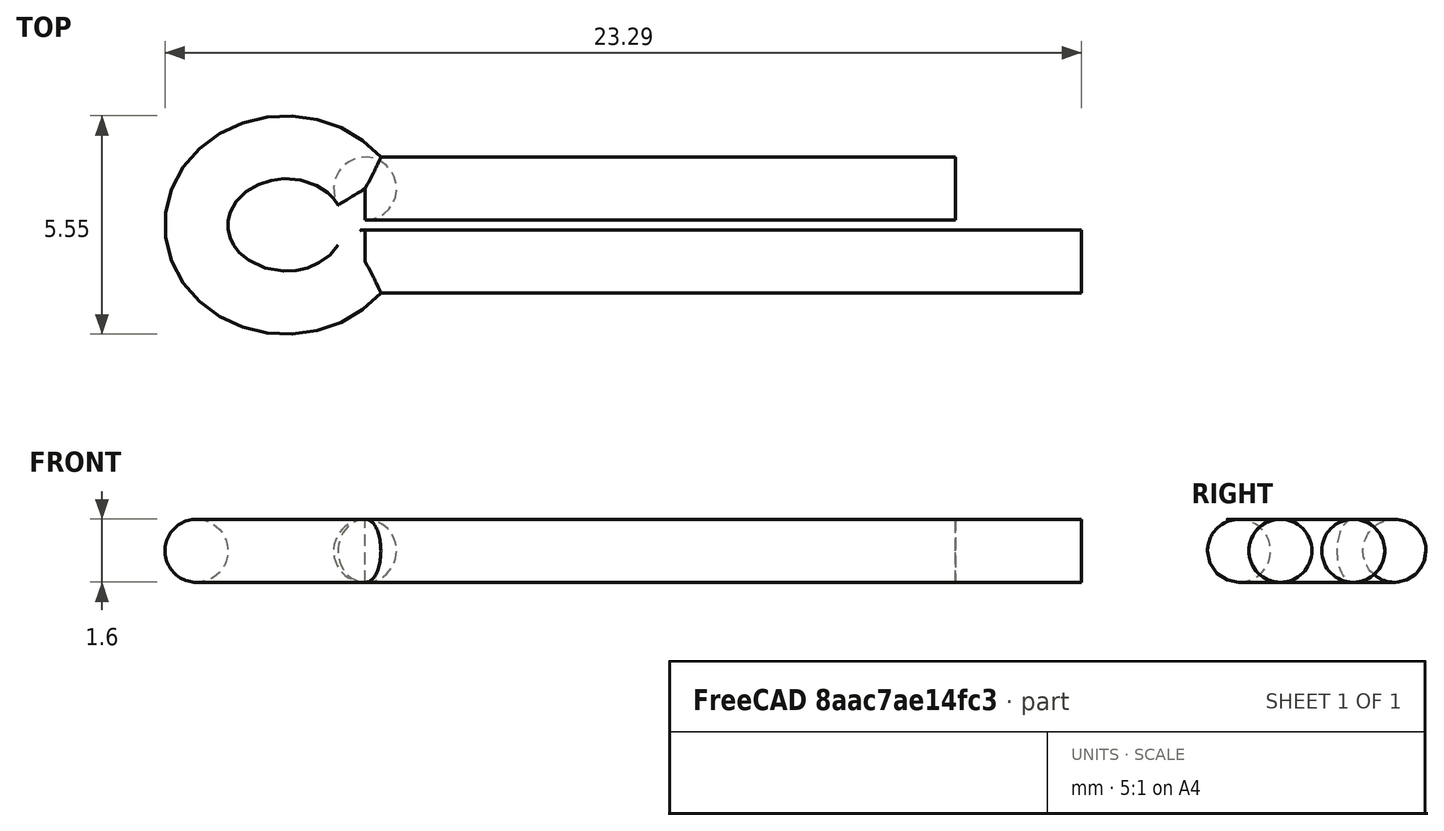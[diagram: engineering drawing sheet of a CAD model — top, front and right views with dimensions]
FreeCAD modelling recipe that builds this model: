
FCSTD DOCUMENT  (FreeCAD 0.17R11586 (Git))
Label: support pin
License: All rights reserved
LicenseURL: http://en.wikipedia.org/wiki/All_rights_reserved
objects: Sketcher::SketchObject×2, PartDesign::Plane×1, PartDesign::AdditivePipe×1, PartDesign::Body×1
note: 6 computed .brp shape members not serialized (recipe doc carries the construction recipe); baked Part::Feature solids carry a one-line shape summary decoded from their .brp

FEATURE [Sketcher::SketchObject] Sketch005
  MapMode = 5
  Placement = pos=(66.3738,51.9691,107.627) rot=(0,0,1;0rad)
  sketch-geometry (7):
    g0: ArcOfEllipse CenterX=-14.3187 CenterY=1.725 CenterZ=0 NormalX=0 NormalY=0 NormalZ=1 MajorRadius=2.275 MinorRadius=1.975 AngleXU=0 StartAngle=0.487427 EndAngle=5.79576
    g1: LineSegment [constr] StartX=-12.0437 StartY=1.725 StartZ=0 EndX=-16.5937 EndY=1.725 EndZ=0
    g2: LineSegment [constr] StartX=-14.3187 StartY=3.7 StartZ=0 EndX=-14.3187 EndY=-0.25 EndZ=0
    g3: GeomPoint X=-13.1895 Y=1.725 Z=0
    g4: GeomPoint X=-15.4478 Y=1.725 Z=0
    g5: LineSegment StartX=-12.3086 StartY=2.65 StartZ=0 EndX=2.6914 EndY=2.65 EndZ=0
    g6: LineSegment StartX=-12.3086 StartY=0.8 StartZ=0 EndX=5.8914 EndY=0.8 EndZ=0
  constraints (13):
    c: InternalAlignment(g1-g4 -> g0) x4
    c: Horizontal(g1)
    c: Horizontal(g5)
    c: Horizontal(g6)
    c: Coincident(g0,g5)
    c: DistanceX(g5,g6) = 3.2
    c: Coincident(g0,g6)
    c: Symmetric(g0,g0,g1)
    c: DistanceY(g0,g2) = 1.975
    c: DistanceX(g1,g0) = 2.275
    c: DistanceY(g6,g5) = 1.85
    c: DistanceX(g5,g5) = 15
    c: DistanceY(g-1,g6) = 0.8
FEATURE [PartDesign::Plane] DatumPlane002
  MapMode = 7
  Placement = pos=(72.2652,52.7691,107.627) rot=(0.57735,-0.57735,-0.57735;2.0944rad)
  Support = -> [Sketch005]
FEATURE [Sketcher::SketchObject] Sketch006
  MapMode = 5
  Placement = pos=(72.2652,52.7691,107.627) rot=(0.57735,-0.57735,-0.57735;2.0944rad)
  Support = -> [DatumPlane002]
  sketch-geometry (1):
    g0: Circle CenterX=0 CenterY=0 CenterZ=0 NormalX=0 NormalY=0 NormalZ=1 Radius=0.8
  constraints (2):
    c: Coincident(g0,g-1)
    c: Radius(g0) = 0.8
FEATURE [PartDesign::AdditivePipe] AdditivePipe
  AuxilleryCurvelinear = true
  AuxillerySpineTangent = false
  Binormal = (0,0,0)
  Mode = 0
  Placement = pos=(72.2652,52.7691,107.627) rot=(0.57735,-0.57735,-0.57735;2.0944rad)
  Profile = -> Sketch006
  Spine = -> Sketch005
  SpineTangent = false
  Transformation = 0
  Transition = 2
FEATURE [PartDesign::Body] Body
  Group = -> [Sketch005,DatumPlane002,Sketch006,AdditivePipe]
  Origin = -> Origin
  Tip = -> AdditivePipe
